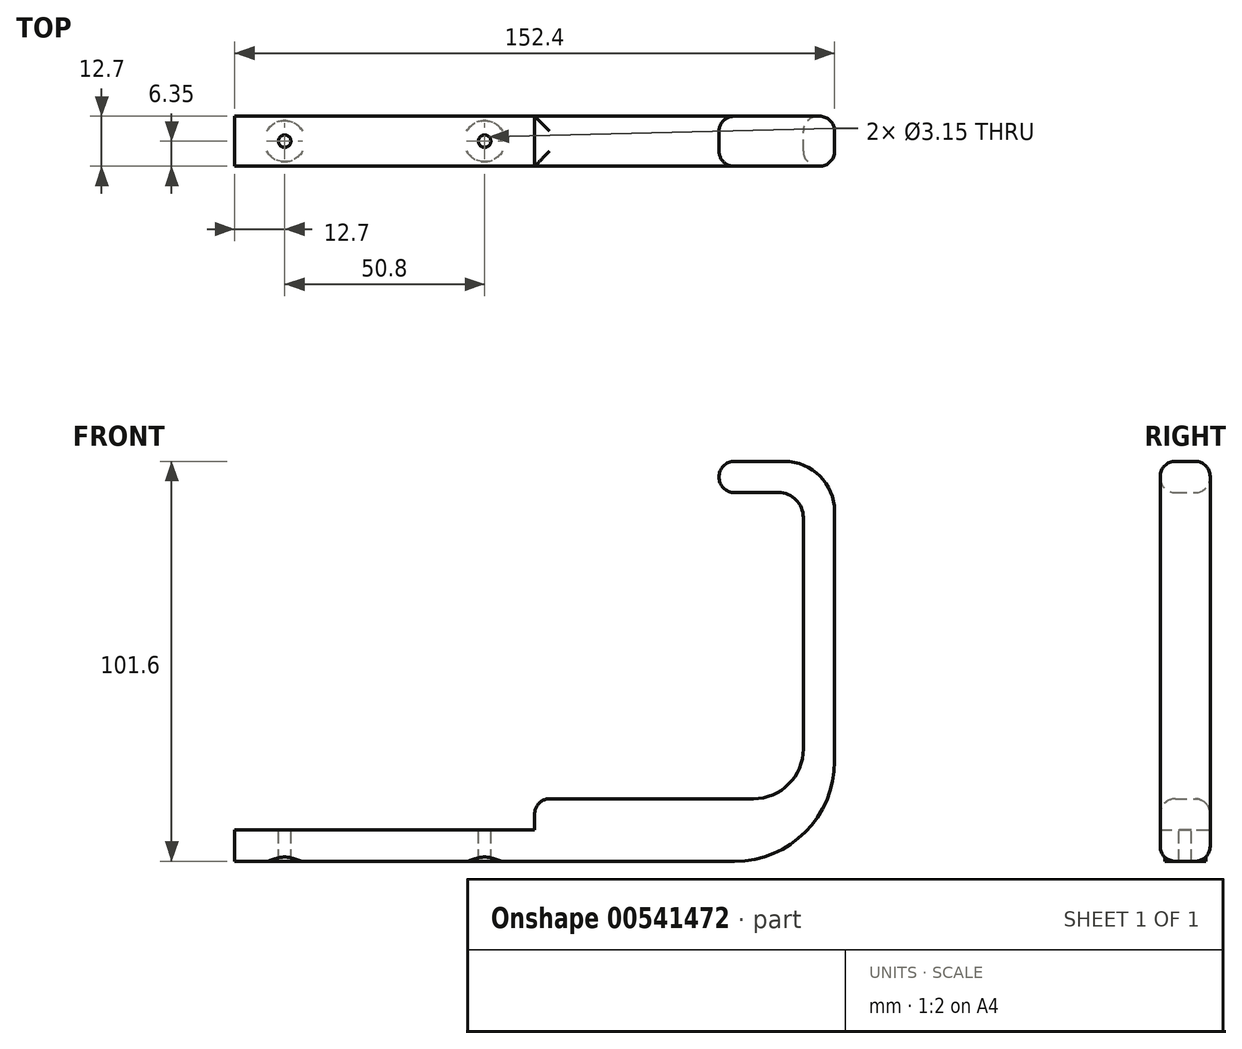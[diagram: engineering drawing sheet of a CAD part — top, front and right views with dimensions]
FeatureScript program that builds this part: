
annotation { "Feature Type Name" : "Feature", "Feature Type Description" : "" }
export const myFeature = defineFeature(function(context is Context, id is Id, definition is map)
    precondition{}
    {
        {
            var Q0;
            Q0=qCreatedBy(makeId("Front.planeOp"),FACE);
            var sketch = newSketch(context, id + "F0", { "sketchPlane" : qUnion([Q0])});
            skLineSegment(sketch, "E0", {"start": v(-18.03, 17.54) * mm, "end": v(-18.03, 25.48) * mm});
            skLineSegment(sketch, "E1", {"start": v(-18.03, 25.48) * mm, "end": v(58.17, 25.48) * mm});
            skLineSegment(sketch, "E2", {"start": v(58.17, 25.48) * mm, "end": v(58.17, 33.42) * mm});
            skLineSegment(sketch, "E3", {"start": v(58.17, 33.42) * mm, "end": v(113.73, 33.42) * mm});
            skLineSegment(sketch, "E4", {"start": v(126.43, 46.12) * mm, "end": v(126.43, 104.86) * mm});
            skLineSegment(sketch, "E5", {"start": v(120.08, 111.2) * mm, "end": v(108.97, 111.2) * mm});
            skLineSegment(sketch, "E6", {"start": v(108.97, 119.14) * mm, "end": v(121.67, 119.14) * mm});
            skLineSegment(sketch, "E7", {"start": v(134.37, 106.44) * mm, "end": v(134.37, 42.94) * mm});
            skLineSegment(sketch, "E8", {"start": v(108.97, 17.54) * mm, "end": v(-18.03, 17.54) * mm});
            skPoint(sketch, "E9.visualSharp", {"position": v(126.43, 111.2) * mm});
            skArc(sketch, "E9.filletArc", {"start": v(126.43, 104.86) * mm, "mid": v(124.57, 109.35) * mm, "end": v(120.08, 111.2) * mm});
            skPoint(sketch, "E10.visualSharp", {"position": v(134.37, 119.14) * mm});
            skArc(sketch, "E10.filletArc", {"start": v(134.37, 106.44) * mm, "mid": v(130.65, 115.42) * mm, "end": v(121.67, 119.14) * mm});
            skPoint(sketch, "E11.visualSharp", {"position": v(134.37, 17.54) * mm});
            skArc(sketch, "E11.filletArc", {"start": v(108.97, 17.54) * mm, "mid": v(126.93, 24.98) * mm, "end": v(134.37, 42.94) * mm});
            skPoint(sketch, "E12.visualSharp", {"position": v(126.43, 33.42) * mm});
            skArc(sketch, "E12.filletArc", {"start": v(113.73, 33.42) * mm, "mid": v(122.71, 37.14) * mm, "end": v(126.43, 46.12) * mm});
            skArc(sketch, "E13", {"start": v(108.97, 119.14) * mm, "mid": v(105, 115.18) * mm, "end": v(108.97, 111.2) * mm});
            skSolve(sketch);
        }
        {
            var Q0;
            Q0=makeQuery(id+"F0.imprint","IMPRINT",FACE,{"disambiguationData":[TD([[makeQuery(id+"F0.imprint","IMPRINT",EDGE,{"derivedFrom":sQuery(id+"F0.wireOp",EDGE,"E0")}),-1.0]])]});
            extrude(context, id + "F1", {"entities" : qUnion([Q0]), "depth" : 12.7 * mm, "offsetDistance" : 25.4 * mm, "symmetric" : true});
        }
        {
            var Q0;
            Q0=makeQuery(id+"F1.opExtrude","SWEPT_FACE",FACE,{"disambiguationData":[OSD([sQuery(id+"F0.wireOp",EDGE,"E1")])]});
            var sketch = newSketch(context, id + "F2", { "sketchPlane" : qUnion([Q0])});
            skCircle(sketch, "E14", {"center": v(45.47, 0) * mm, "radius": 1.57 * mm});
            skCircle(sketch, "E15", {"center": v(-5.33, 0) * mm, "radius": 1.57 * mm});
            skSolve(sketch);
        }
        {
            var Q0;
            Q0 = qSketchRegion(id + "F2", true);
            extrude(context, id + "F3", {"entities" : qUnion([Q0]), "operationType" : NewBodyOperationType.REMOVE, "endBound" : BoundingType.THROUGH_ALL, "oppositeDirection" : true, "depth" : 25.4 * mm, "offsetDistance" : 25.4 * mm});
        }
        {
            var Q0;
            Q0=makeQuery(id+"F1.opExtrude","CAP_EDGE",EDGE,{"disambiguationData":[OSD([sQuery(id+"F0.wireOp",EDGE,"E4")])],"isStart":true});
            var Q1;
            Q1=makeQuery(id+"F1.opExtrude","CAP_EDGE",EDGE,{"disambiguationData":[OSD([sQuery(id+"F0.wireOp",EDGE,"E4")])],"isStart":false});
            var Q2;
            Q2=makeQuery(id+"F1.opExtrude","CAP_EDGE",EDGE,{"disambiguationData":[OSD([sQuery(id+"F0.wireOp",EDGE,"E9.filletArc")])],"isStart":false});
            var Q3;
            Q3=makeQuery(id+"F1.opExtrude","CAP_EDGE",EDGE,{"disambiguationData":[OSD([sQuery(id+"F0.wireOp",EDGE,"E9.filletArc")])],"isStart":true});
            var Q4;
            Q4=makeQuery(id+"F1.opExtrude","CAP_EDGE",EDGE,{"disambiguationData":[OSD([sQuery(id+"F0.wireOp",EDGE,"E12.filletArc")])],"isStart":false});
            var Q5;
            Q5=makeQuery(id+"F1.opExtrude","CAP_EDGE",EDGE,{"disambiguationData":[OSD([sQuery(id+"F0.wireOp",EDGE,"E12.filletArc")])],"isStart":true});
            var Q6;
            Q6=makeQuery(id+"F1.opExtrude","CAP_EDGE",EDGE,{"disambiguationData":[OSD([sQuery(id+"F0.wireOp",EDGE,"E3")])],"isStart":true});
            var Q7;
            Q7=makeQuery(id+"F1.opExtrude","CAP_EDGE",EDGE,{"disambiguationData":[OSD([sQuery(id+"F0.wireOp",EDGE,"E3")])],"isStart":false});
            var Q8;
            Q8=makeQuery(id+"F1.opExtrude","SWEPT_EDGE",EDGE,{"disambiguationData":[OSD([sQuery(id+"F0.wireOp",EDGE,"E2"),sQuery(id+"F0.wireOp",EDGE,"E3")])]});
            var Q9;
            Q9=makeQuery(id+"F1.opExtrude","CAP_EDGE",EDGE,{"disambiguationData":[OSD([sQuery(id+"F0.wireOp",EDGE,"E5")])],"isStart":true});
            var Q10;
            Q10=makeQuery(id+"F1.opExtrude","CAP_EDGE",EDGE,{"disambiguationData":[OSD([sQuery(id+"F0.wireOp",EDGE,"E5")])],"isStart":false});
            var Q11;
            Q11=makeQuery(id+"F1.opExtrude","CAP_EDGE",EDGE,{"disambiguationData":[OSD([sQuery(id+"F0.wireOp",EDGE,"E13")])],"isStart":false});
            var Q12;
            Q12=makeQuery(id+"F1.opExtrude","CAP_EDGE",EDGE,{"disambiguationData":[OSD([sQuery(id+"F0.wireOp",EDGE,"E13")])],"isStart":true});
            var Q13;
            Q13=makeQuery(id+"F1.opExtrude","CAP_EDGE",EDGE,{"disambiguationData":[OSD([sQuery(id+"F0.wireOp",EDGE,"E6")])],"isStart":true});
            var Q14;
            Q14=makeQuery(id+"F1.opExtrude","CAP_EDGE",EDGE,{"disambiguationData":[OSD([sQuery(id+"F0.wireOp",EDGE,"E6")])],"isStart":false});
            var Q15;
            Q15=makeQuery(id+"F1.opExtrude","CAP_EDGE",EDGE,{"disambiguationData":[OSD([sQuery(id+"F0.wireOp",EDGE,"E10.filletArc")])],"isStart":true});
            var Q16;
            Q16=makeQuery(id+"F1.opExtrude","CAP_EDGE",EDGE,{"disambiguationData":[OSD([sQuery(id+"F0.wireOp",EDGE,"E7")])],"isStart":true});
            var Q17;
            Q17=makeQuery(id+"F1.opExtrude","CAP_EDGE",EDGE,{"disambiguationData":[OSD([sQuery(id+"F0.wireOp",EDGE,"E7")])],"isStart":false});
            var Q18;
            Q18=makeQuery(id+"F1.opExtrude","CAP_EDGE",EDGE,{"disambiguationData":[OSD([sQuery(id+"F0.wireOp",EDGE,"E10.filletArc")])],"isStart":false});
            var Q19;
            Q19=makeQuery(id+"F1.opExtrude","CAP_EDGE",EDGE,{"disambiguationData":[OSD([sQuery(id+"F0.wireOp",EDGE,"E11.filletArc")])],"isStart":true});
            var Q20;
            Q20=makeQuery(id+"F1.opExtrude","CAP_EDGE",EDGE,{"disambiguationData":[OSD([sQuery(id+"F0.wireOp",EDGE,"E11.filletArc")])],"isStart":false});
            var Q21;
            Q21=makeQuery(id+"F1.opExtrude","CAP_EDGE",EDGE,{"disambiguationData":[OSD([sQuery(id+"F0.wireOp",EDGE,"E8")])],"isStart":true});
            var Q22;
            Q22=makeQuery(id+"F1.opExtrude","CAP_EDGE",EDGE,{"disambiguationData":[OSD([sQuery(id+"F0.wireOp",EDGE,"E8")])],"isStart":false});
            fillet(context, id + "F4", {"entities" : qUnion([Q0, Q1, Q2, Q3, Q4, Q5, Q6, Q7, Q8, Q9, Q10, Q11, Q12, Q13, Q14, Q15, Q16, Q17, Q18, Q19, Q20, Q21, Q22]), "radius" : 3.8 * mm, "allowEdgeOverflow" : false});
        }
        {
            var Q0;
            Q0=makeQuery(id+"F1.opExtrude","SWEPT_FACE",FACE,{"disambiguationData":[OSD([sQuery(id+"F0.wireOp",EDGE,"E8")])]});
            var sketch = newSketch(context, id + "F5", { "sketchPlane" : qUnion([Q0])});
            skCircle(sketch, "E16", {"center": v(-5.33, 0) * mm, "radius": 1.64 * mm});
            skCircle(sketch, "E17", {"center": v(-5.33, 0) * mm, "radius": 5.2 * mm});
            skCircle(sketch, "E18", {"center": v(45.47, 0) * mm, "radius": 1.61 * mm});
            skCircle(sketch, "E19", {"center": v(45.47, 0) * mm, "radius": 5.2 * mm});
            skSolve(sketch);
        }
        {
            var Q0;
            Q0 = qSketchRegion(id + "F5", true);
            extrude(context, id + "F6", {"entities" : qUnion([Q0]), "operationType" : NewBodyOperationType.ADD, "endBound" : BoundingType.UP_TO_NEXT, "oppositeDirection" : true, "depth" : 25.4 * mm, "offsetDistance" : 25.4 * mm});
        }
    });
